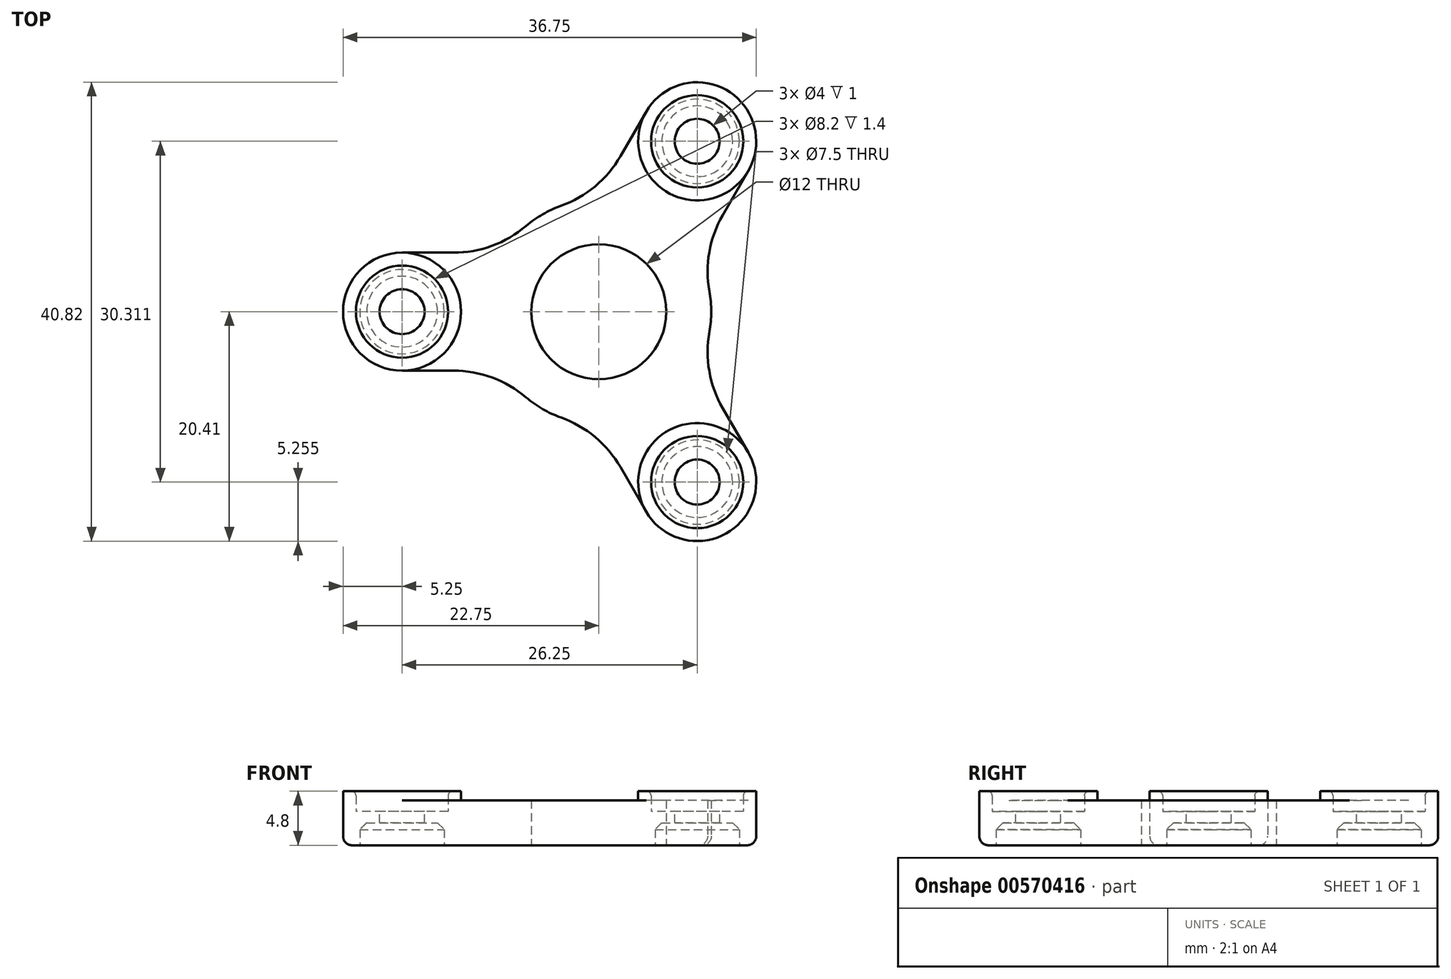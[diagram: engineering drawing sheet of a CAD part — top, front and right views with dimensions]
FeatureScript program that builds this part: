
annotation { "Feature Type Name" : "Feature", "Feature Type Description" : "" }
export const myFeature = defineFeature(function(context is Context, id is Id, definition is map)
    precondition{}
    {
        {
            var Q0;
            Q0=qCreatedBy(makeId("Top.planeOp"),FACE);
            var sketch = newSketch(context, id + "F0", { "sketchPlane" : qUnion([Q0])});
            skArc(sketch, "E0", {"start": v(-17.5, 0) * mm, "mid": v(8.75, -15.16) * mm, "end": v(8.75, 15.16) * mm, "construction": true});
            skLineSegment(sketch, "E1", {"start": v(-17.5, 0) * mm, "end": v(17.5, 0) * mm, "construction": true});
            skLineSegment(sketch, "E2", {"start": v(0, 17.5) * mm, "end": v(0, -17.5) * mm, "construction": true});
            skCircle(sketch, "E3", {"center": v(-17.5, 0) * mm, "radius": 11 * mm, "construction": true});
            skCircle(sketch, "E4", {"center": v(0, 0) * mm, "radius": 10 * mm});
            skCircle(sketch, "E5", {"center": v(-17.5, 0) * mm, "radius": 5.25 * mm});
            skPoint(sketch, "E6.center", {"position": v(-0.38, 0.43) * mm});
            skPoint(sketch, "E7.center", {"position": v(0.72, 3.29) * mm});
            skCircle(sketch, "E8", {"center": v(0, 0) * mm, "radius": 28.5 * mm, "construction": true});
            skPoint(sketch, "E9.orphan", {"position": v(-2.14, 9.77) * mm});
            skPoint(sketch, "E10.orphan", {"position": v(18.22, 8.85) * mm});
            skPoint(sketch, "E11.orphan", {"position": v(12.53, 1.01) * mm});
            skPoint(sketch, "E12.orphan", {"position": v(-7.15, -5.8) * mm});
            skPoint(sketch, "E13.orphan", {"position": v(-2.14, -9.77) * mm});
            skCircle(sketch, "E14", {"center": v(0, 0) * mm, "radius": 6 * mm});
            skArc(sketch, "E15.trimOffspring", {"start": v(2.11, 17.37) * mm, "mid": v(-9.5, 14.7) * mm, "end": v(-16.71, 5.2) * mm, "construction": true});
            skLineSegment(sketch, "E16", {"start": v(-17.5, 0) * mm, "end": v(-17.5, 5.25) * mm, "construction": true});
            skLineSegment(sketch, "E17", {"start": v(-17.5, 5.25) * mm, "end": v(-8.51, 5.25) * mm});
            skLineSegment(sketch, "E18.MirrorCS", {"start": v(-17.5, -5.25) * mm, "end": v(-8.51, -5.25) * mm});
            skCircle(sketch, "E19.1.0", {"center": v(8.75, -15.16) * mm, "radius": 11 * mm, "construction": true});
            skCircle(sketch, "E19.1.1", {"center": v(8.75, -15.16) * mm, "radius": 5.25 * mm});
            skLineSegment(sketch, "E19.1.2", {"start": v(13.3, -12.53) * mm, "end": v(8.8, -4.75) * mm});
            skLineSegment(sketch, "E19.1.3", {"start": v(4.2, -17.78) * mm, "end": v(-0.3, -10) * mm});
            skLineSegment(sketch, "E19.1.4", {"start": v(8.75, -15.16) * mm, "end": v(-8.75, 15.16) * mm, "construction": true});
            skCircle(sketch, "E19.2.0", {"center": v(8.75, 15.16) * mm, "radius": 11 * mm, "construction": true});
            skCircle(sketch, "E19.2.1", {"center": v(8.75, 15.16) * mm, "radius": 5.25 * mm});
            skLineSegment(sketch, "E19.2.2", {"start": v(4.2, 17.78) * mm, "end": v(-0.3, 10) * mm});
            skLineSegment(sketch, "E19.2.3", {"start": v(13.3, 12.53) * mm, "end": v(8.8, 4.75) * mm});
            skLineSegment(sketch, "E19.2.4", {"start": v(8.75, 15.16) * mm, "end": v(-8.75, -15.16) * mm, "construction": true});
            skSolve(sketch);
        }
        {
            var Q0;
            Q0=makeQuery(id+"F0.imprint","IMPRINT",FACE,{"disambiguationData":[TD([[makeQuery(id+"F0.imprint","IMPRINT",EDGE,{"derivedFrom":sQuery(id+"F0.wireOp",EDGE,"E14")}),-1.0]])]});
            var Q1;
            {var subQ0=sQuery(id+"F0.wireOp",EDGE,"E17");Q1=makeQuery(id+"F0.imprint","IMPRINT",FACE,{"disambiguationData":[TD([[makeQuery(id+"F0.imprint","IMPRINT",EDGE,{"derivedFrom":subQ0}),-1.0]])]});}
            var Q2;
            {var subQ0=sQuery(id+"F0.wireOp",EDGE,"E5");var subQ1=makeQuery(id+"F0.imprint","INTERSECT",VERTEX,{"derivedFrom":[subQ0,sQuery(id+"F0.wireOp",EDGE,"E17")]});Q2=makeQuery(id+"F0.imprint","IMPRINT",FACE,{"disambiguationData":[TD([[makeQuery(id+"F0.imprint","IMPRINT",EDGE,{"disambiguationData":[TD([[subQ1,-1.0]])],"derivedFrom":subQ0}),1.0]])]});}
            var Q3;
            {var subQ0=sQuery(id+"F0.wireOp",EDGE,"E19.2.1");var subQ1=makeQuery(id+"F0.imprint","INTERSECT",VERTEX,{"derivedFrom":[subQ0,sQuery(id+"F0.wireOp",EDGE,"E19.2.2")]});Q3=makeQuery(id+"F0.imprint","IMPRINT",FACE,{"disambiguationData":[TD([[makeQuery(id+"F0.imprint","IMPRINT",EDGE,{"disambiguationData":[TD([[subQ1,1.0]])],"derivedFrom":subQ0}),1.0]])]});}
            var Q4;
            {var subQ0=sQuery(id+"F0.wireOp",EDGE,"E19.2.2");Q4=makeQuery(id+"F0.imprint","IMPRINT",FACE,{"disambiguationData":[TD([[makeQuery(id+"F0.imprint","IMPRINT",EDGE,{"derivedFrom":subQ0}),1.0]])]});}
            var Q5;
            {var subQ0=sQuery(id+"F0.wireOp",EDGE,"E19.1.2");Q5=makeQuery(id+"F0.imprint","IMPRINT",FACE,{"disambiguationData":[TD([[makeQuery(id+"F0.imprint","IMPRINT",EDGE,{"derivedFrom":subQ0}),1.0]])]});}
            var Q6;
            {var subQ0=sQuery(id+"F0.wireOp",EDGE,"E19.1.1");var subQ1=makeQuery(id+"F0.imprint","INTERSECT",VERTEX,{"derivedFrom":[subQ0,sQuery(id+"F0.wireOp",EDGE,"E19.1.2")]});Q6=makeQuery(id+"F0.imprint","IMPRINT",FACE,{"disambiguationData":[TD([[makeQuery(id+"F0.imprint","IMPRINT",EDGE,{"disambiguationData":[TD([[subQ1,1.0]])],"derivedFrom":subQ0}),1.0]])]});}
            extrude(context, id + "F1", {"entities" : qUnion([Q0, Q1, Q2, Q3, Q4, Q5, Q6]), "depth" : 4 * mm, "offsetDistance" : 25 * mm});
        }
        {
            var Q0;
            Q0=makeQuery(id+"F1.opExtrude","CAP_FACE",FACE,{"disambiguationData":[OSD([sQuery(id+"F0.wireOp",EDGE,"E4"),sQuery(id+"F0.wireOp",EDGE,"E5"),sQuery(id+"F0.wireOp",EDGE,"E6.1.0"),sQuery(id+"F0.wireOp",EDGE,"E6.2.0"),sQuery(id+"F0.wireOp",EDGE,"E14"),sQuery(id+"F0.wireOp",EDGE,"E17"),sQuery(id+"F0.wireOp",EDGE,"E18.MirrorCS"),sQuery(id+"F0.wireOp",EDGE,"43669a28-cf5b-415e-ac1e-aebf97da9a9c.1.0"),sQuery(id+"F0.wireOp",EDGE,"43669a28-cf5b-415e-ac1e-aebf97da9a9c.1.1"),sQuery(id+"F0.wireOp",EDGE,"43669a28-cf5b-415e-ac1e-aebf97da9a9c.2.0"),sQuery(id+"F0.wireOp",EDGE,"43669a28-cf5b-415e-ac1e-aebf97da9a9c.2.1")])],"isStart":false});
            var sketch = newSketch(context, id + "F2", { "sketchPlane" : qUnion([Q0])});
            skCircle(sketch, "E20.0", {"center": v(-17.5, 0) * mm, "radius": 5.25 * mm});
            skCircle(sketch, "E21", {"center": v(-17.5, 0) * mm, "radius": 4.1 * mm});
            skCircle(sketch, "E22.1.0", {"center": v(8.75, -15.16) * mm, "radius": 5.25 * mm});
            skCircle(sketch, "E22.1.1", {"center": v(8.75, -15.16) * mm, "radius": 4.1 * mm});
            skCircle(sketch, "E22.2.0", {"center": v(8.75, 15.16) * mm, "radius": 5.25 * mm});
            skCircle(sketch, "E22.2.1", {"center": v(8.75, 15.16) * mm, "radius": 4.1 * mm});
            skPoint(sketch, "E22.center", {"position": v(0, 0) * mm});
            skCircle(sketch, "E23", {"center": v(-17.5, 0) * mm, "radius": 2 * mm});
            skCircle(sketch, "E24.1.0", {"center": v(8.75, -15.16) * mm, "radius": 2 * mm});
            skCircle(sketch, "E24.2.0", {"center": v(8.75, 15.16) * mm, "radius": 2 * mm});
            skSolve(sketch);
        }
        {
            var Q0;
            Q0=makeQuery(id+"F2.imprint","IMPRINT",FACE,{"disambiguationData":[TD([[makeQuery(id+"F2.imprint","IMPRINT",EDGE,{"derivedFrom":sQuery(id+"F2.wireOp",EDGE,"E21")}),-1.0]])]});
            var Q1;
            Q1=makeQuery(id+"F2.imprint","IMPRINT",FACE,{"disambiguationData":[TD([[makeQuery(id+"F2.imprint","IMPRINT",EDGE,{"derivedFrom":sQuery(id+"F2.wireOp",EDGE,"E22.2.0")}),1.0]])]});
            var Q2;
            Q2=makeQuery(id+"F2.imprint","IMPRINT",FACE,{"disambiguationData":[TD([[makeQuery(id+"F2.imprint","IMPRINT",EDGE,{"derivedFrom":sQuery(id+"F2.wireOp",EDGE,"E22.1.0")}),1.0]])]});
            extrude(context, id + "F3", {"entities" : qUnion([Q0, Q1, Q2]), "operationType" : NewBodyOperationType.ADD, "depth" : .8 * mm, "offsetDistance" : 25 * mm});
        }
        {
            var Q0;
            Q0=makeQuery(id+"F2.imprint","IMPRINT",FACE,{"disambiguationData":[TD([[makeQuery(id+"F2.imprint","IMPRINT",EDGE,{"derivedFrom":sQuery(id+"F2.wireOp",EDGE,"E23")}),1.0]])]});
            var Q1;
            Q1=makeQuery(id+"F2.imprint","IMPRINT",FACE,{"disambiguationData":[TD([[makeQuery(id+"F2.imprint","IMPRINT",EDGE,{"derivedFrom":sQuery(id+"F2.wireOp",EDGE,"E24.2.0")}),1.0]])]});
            var Q2;
            Q2=makeQuery(id+"F2.imprint","IMPRINT",FACE,{"disambiguationData":[TD([[makeQuery(id+"F2.imprint","IMPRINT",EDGE,{"derivedFrom":sQuery(id+"F2.wireOp",EDGE,"E24.1.0")}),1.0]])]});
            extrude(context, id + "F4", {"entities" : qUnion([Q0, Q1, Q2]), "operationType" : NewBodyOperationType.REMOVE, "endBound" : BoundingType.THROUGH_ALL, "oppositeDirection" : true, "depth" : 25 * mm, "offsetDistance" : 25 * mm});
        }
        {
            var Q0;
            Q0=makeQuery(id+"F1.opExtrude","CAP_FACE",FACE,{"disambiguationData":[OSD([sQuery(id+"F0.wireOp",EDGE,"E4"),sQuery(id+"F0.wireOp",EDGE,"E5"),sQuery(id+"F0.wireOp",EDGE,"E6.1.0"),sQuery(id+"F0.wireOp",EDGE,"E6.2.0"),sQuery(id+"F0.wireOp",EDGE,"E14"),sQuery(id+"F0.wireOp",EDGE,"E17"),sQuery(id+"F0.wireOp",EDGE,"E18.MirrorCS"),sQuery(id+"F0.wireOp",EDGE,"43669a28-cf5b-415e-ac1e-aebf97da9a9c.1.0"),sQuery(id+"F0.wireOp",EDGE,"43669a28-cf5b-415e-ac1e-aebf97da9a9c.1.1"),sQuery(id+"F0.wireOp",EDGE,"43669a28-cf5b-415e-ac1e-aebf97da9a9c.2.0"),sQuery(id+"F0.wireOp",EDGE,"43669a28-cf5b-415e-ac1e-aebf97da9a9c.2.1")])],"isStart":true});
            var sketch = newSketch(context, id + "F5", { "sketchPlane" : qUnion([Q0])});
            skCircle(sketch, "E25.0", {"center": v(-17.5, 0) * mm, "radius": 2 * mm, "construction": true});
            skCircle(sketch, "E26", {"center": v(-17.5, 0) * mm, "radius": 3.75 * mm});
            skCircle(sketch, "E27.1.0", {"center": v(8.75, -15.16) * mm, "radius": 3.75 * mm});
            skCircle(sketch, "E27.2.0", {"center": v(8.75, 15.16) * mm, "radius": 3.75 * mm});
            skPoint(sketch, "E27.center", {"position": v(0, 0) * mm});
            skSolve(sketch);
        }
        {
            var Q0;
            Q0=makeQuery(id+"F5.imprint","IMPRINT",FACE,{"disambiguationData":[TD([[makeQuery(id+"F5.imprint","IMPRINT",EDGE,{"derivedFrom":sQuery(id+"F5.wireOp",EDGE,"E26")}),1.0]])]});
            var Q1;
            Q1=makeQuery(id+"F5.imprint","IMPRINT",FACE,{"disambiguationData":[TD([[makeQuery(id+"F5.imprint","IMPRINT",EDGE,{"derivedFrom":sQuery(id+"F5.wireOp",EDGE,"E27.2.0")}),1.0]])]});
            var Q2;
            Q2=makeQuery(id+"F5.imprint","IMPRINT",FACE,{"disambiguationData":[TD([[makeQuery(id+"F5.imprint","IMPRINT",EDGE,{"derivedFrom":sQuery(id+"F5.wireOp",EDGE,"E27.1.0")}),1.0]])]});
            extrude(context, id + "F6", {"entities" : qUnion([Q0, Q1, Q2]), "operationType" : NewBodyOperationType.REMOVE, "oppositeDirection" : true, "depth" : 2 * mm, "offsetDistance" : 25 * mm});
        }
        {
            var Q0;
            Q0=makeQuery(id+"F6.boolean.opBoolean","COPY",EDGE,{"derivedFrom":makeQuery(id+"F6.opExtrude","CAP_EDGE",EDGE,{"disambiguationData":[OSD([sQuery(id+"F5.wireOp",EDGE,"E27.2.0")])],"isStart":false})});
            var Q1;
            Q1=makeQuery(id+"F6.boolean.opBoolean","COPY",EDGE,{"derivedFrom":makeQuery(id+"F6.opExtrude","CAP_EDGE",EDGE,{"disambiguationData":[OSD([sQuery(id+"F5.wireOp",EDGE,"E26")])],"isStart":false})});
            var Q2;
            Q2=makeQuery(id+"F6.boolean.opBoolean","COPY",EDGE,{"derivedFrom":makeQuery(id+"F6.opExtrude","CAP_EDGE",EDGE,{"disambiguationData":[OSD([sQuery(id+"F5.wireOp",EDGE,"E27.1.0")])],"isStart":false})});
            chamfer(context, id + "F7", {"entities" : qUnion([Q0, Q1, Q2]), "width" : .6 * mm, "tangentPropagation" : true});
        }
        {
            var Q0;
            Q0=makeQuery(id+"F3.boolean.opBoolean","SPLIT",FACE,{"disambiguationData":[TD([makeQuery(id+"F3.opExtrude","SWEPT_FACE",FACE,{"disambiguationData":[OSD([sQuery(id+"F2.wireOp",EDGE,"E21")])]})])],"derivedFrom":makeQuery(id+"F1.opExtrude","CAP_FACE",FACE,{"disambiguationData":[OSD([sQuery(id+"F0.wireOp",EDGE,"E4"),sQuery(id+"F0.wireOp",EDGE,"E5"),sQuery(id+"F0.wireOp",EDGE,"E6.1.0"),sQuery(id+"F0.wireOp",EDGE,"E6.2.0"),sQuery(id+"F0.wireOp",EDGE,"E14"),sQuery(id+"F0.wireOp",EDGE,"E17"),sQuery(id+"F0.wireOp",EDGE,"E18.MirrorCS"),sQuery(id+"F0.wireOp",EDGE,"43669a28-cf5b-415e-ac1e-aebf97da9a9c.1.0"),sQuery(id+"F0.wireOp",EDGE,"43669a28-cf5b-415e-ac1e-aebf97da9a9c.1.1"),sQuery(id+"F0.wireOp",EDGE,"43669a28-cf5b-415e-ac1e-aebf97da9a9c.2.0"),sQuery(id+"F0.wireOp",EDGE,"43669a28-cf5b-415e-ac1e-aebf97da9a9c.2.1")])],"isStart":false})});
            var Q1;
            Q1=makeQuery(id+"F3.boolean.opBoolean","SPLIT",FACE,{"disambiguationData":[TD([makeQuery(id+"F3.opExtrude","SWEPT_FACE",FACE,{"disambiguationData":[OSD([sQuery(id+"F2.wireOp",EDGE,"E22.2.1")])]})])],"derivedFrom":makeQuery(id+"F1.opExtrude","CAP_FACE",FACE,{"disambiguationData":[OSD([sQuery(id+"F0.wireOp",EDGE,"E4"),sQuery(id+"F0.wireOp",EDGE,"E5"),sQuery(id+"F0.wireOp",EDGE,"E6.1.0"),sQuery(id+"F0.wireOp",EDGE,"E6.2.0"),sQuery(id+"F0.wireOp",EDGE,"E14"),sQuery(id+"F0.wireOp",EDGE,"E17"),sQuery(id+"F0.wireOp",EDGE,"E18.MirrorCS"),sQuery(id+"F0.wireOp",EDGE,"43669a28-cf5b-415e-ac1e-aebf97da9a9c.1.0"),sQuery(id+"F0.wireOp",EDGE,"43669a28-cf5b-415e-ac1e-aebf97da9a9c.1.1"),sQuery(id+"F0.wireOp",EDGE,"43669a28-cf5b-415e-ac1e-aebf97da9a9c.2.0"),sQuery(id+"F0.wireOp",EDGE,"43669a28-cf5b-415e-ac1e-aebf97da9a9c.2.1")])],"isStart":false})});
            var Q2;
            Q2=makeQuery(id+"F3.boolean.opBoolean","SPLIT",FACE,{"disambiguationData":[TD([makeQuery(id+"F3.opExtrude","SWEPT_FACE",FACE,{"disambiguationData":[OSD([sQuery(id+"F2.wireOp",EDGE,"E22.1.1")])]})])],"derivedFrom":makeQuery(id+"F1.opExtrude","CAP_FACE",FACE,{"disambiguationData":[OSD([sQuery(id+"F0.wireOp",EDGE,"E4"),sQuery(id+"F0.wireOp",EDGE,"E5"),sQuery(id+"F0.wireOp",EDGE,"E6.1.0"),sQuery(id+"F0.wireOp",EDGE,"E6.2.0"),sQuery(id+"F0.wireOp",EDGE,"E14"),sQuery(id+"F0.wireOp",EDGE,"E17"),sQuery(id+"F0.wireOp",EDGE,"E18.MirrorCS"),sQuery(id+"F0.wireOp",EDGE,"43669a28-cf5b-415e-ac1e-aebf97da9a9c.1.0"),sQuery(id+"F0.wireOp",EDGE,"43669a28-cf5b-415e-ac1e-aebf97da9a9c.1.1"),sQuery(id+"F0.wireOp",EDGE,"43669a28-cf5b-415e-ac1e-aebf97da9a9c.2.0"),sQuery(id+"F0.wireOp",EDGE,"43669a28-cf5b-415e-ac1e-aebf97da9a9c.2.1")])],"isStart":false})});
            extrude(context, id + "F8", {"entities" : qUnion([Q0, Q1, Q2]), "operationType" : NewBodyOperationType.REMOVE, "oppositeDirection" : true, "depth" : 1 * mm, "offsetDistance" : 25 * mm});
        }
        {
            var Q0;
            Q0=makeQuery(id+"F1.opExtrude","SWEPT_EDGE",EDGE,{"disambiguationData":[OSD([sQuery(id+"F0.wireOp",EDGE,"E4"),sQuery(id+"F0.wireOp",EDGE,"E18.MirrorCS")])]});
            var Q1;
            Q1=makeQuery(id+"F1.opExtrude","SWEPT_EDGE",EDGE,{"disambiguationData":[OSD([sQuery(id+"F0.wireOp",EDGE,"E4"),sQuery(id+"F0.wireOp",EDGE,"43669a28-cf5b-415e-ac1e-aebf97da9a9c.1.0")])]});
            var Q2;
            Q2=makeQuery(id+"F1.opExtrude","SWEPT_EDGE",EDGE,{"disambiguationData":[OSD([sQuery(id+"F0.wireOp",EDGE,"E4"),sQuery(id+"F0.wireOp",EDGE,"43669a28-cf5b-415e-ac1e-aebf97da9a9c.1.1")])]});
            var Q3;
            Q3=makeQuery(id+"F1.opExtrude","SWEPT_EDGE",EDGE,{"disambiguationData":[OSD([sQuery(id+"F0.wireOp",EDGE,"E4"),sQuery(id+"F0.wireOp",EDGE,"43669a28-cf5b-415e-ac1e-aebf97da9a9c.2.0")])]});
            var Q4;
            Q4=makeQuery(id+"F1.opExtrude","SWEPT_EDGE",EDGE,{"disambiguationData":[OSD([sQuery(id+"F0.wireOp",EDGE,"E4"),sQuery(id+"F0.wireOp",EDGE,"E17")])]});
            var Q5;
            Q5=makeQuery(id+"F1.opExtrude","SWEPT_EDGE",EDGE,{"disambiguationData":[OSD([sQuery(id+"F0.wireOp",EDGE,"E4"),sQuery(id+"F0.wireOp",EDGE,"43669a28-cf5b-415e-ac1e-aebf97da9a9c.2.1")])]});
            fillet(context, id + "F9", {"entities" : qUnion([Q0, Q1, Q2, Q3, Q4, Q5]), "radius" : 10 * mm, "tangentPropagation" : true, "allowEdgeOverflow" : false});
        }
        {
            var Q0;
            {var subQ0=sQuery(id+"F0.wireOp",EDGE,"E18.MirrorCS");var subQ1=sQuery(id+"F0.wireOp",EDGE,"E17");var subQ2=sQuery(id+"F0.wireOp",EDGE,"E14");var subQ3=sQuery(id+"F0.wireOp",EDGE,"E6.2.0");var subQ4=sQuery(id+"F0.wireOp",EDGE,"E6.1.0");var subQ5=sQuery(id+"F0.wireOp",EDGE,"43669a28-cf5b-415e-ac1e-aebf97da9a9c.1.0");var subQ6=sQuery(id+"F0.wireOp",EDGE,"E4");var subQ7=sQuery(id+"F0.wireOp",EDGE,"43669a28-cf5b-415e-ac1e-aebf97da9a9c.2.1");var subQ8=sQuery(id+"F0.wireOp",EDGE,"E5");var subQ9=sQuery(id+"F0.wireOp",EDGE,"43669a28-cf5b-415e-ac1e-aebf97da9a9c.1.1");var subQ10=sQuery(id+"F0.wireOp",EDGE,"43669a28-cf5b-415e-ac1e-aebf97da9a9c.2.0");Q0=makeQuery(id+"F3.boolean.opBoolean","SPLIT",FACE,{"disambiguationData":[TD([makeQuery(id+"F1.opExtrude","SWEPT_FACE",FACE,{"disambiguationData":[OSD([subQ8])]})])],"derivedFrom":makeQuery(id+"F1.opExtrude","CAP_FACE",FACE,{"disambiguationData":[OSD([subQ6,subQ8,subQ4,subQ3,subQ2,subQ1,subQ0,subQ5,subQ9,subQ10,subQ7])],"isStart":false})});}
            var Q1;
            Q1=makeQuery(id+"F3.opExtrude","CAP_EDGE",EDGE,{"disambiguationData":[OSD([sQuery(id+"F2.wireOp",EDGE,"E21")])],"isStart":false});
            var Q2;
            Q2=makeQuery(id+"F3.opExtrude","CAP_EDGE",EDGE,{"disambiguationData":[OSD([sQuery(id+"F2.wireOp",EDGE,"E22.1.1")])],"isStart":false});
            var Q3;
            Q3=makeQuery(id+"F3.opExtrude","CAP_EDGE",EDGE,{"disambiguationData":[OSD([sQuery(id+"F2.wireOp",EDGE,"E22.2.1")])],"isStart":false});
            fillet(context, id + "F10", {"entities" : qUnion([Q0, Q1, Q2, Q3]), "radius" : .4 * mm, "tangentPropagation" : true, "allowEdgeOverflow" : false});
        }
        {
            var Q0;
            {var subQ0=sQuery(id+"F0.wireOp",EDGE,"E18.MirrorCS");var subQ1=sQuery(id+"F0.wireOp",EDGE,"E4");Q0=makeQuery(id+"F9.opFillet","BLEND_EDGE",EDGE,{"blendedFrom":[makeQuery(id+"F1.opExtrude","SWEPT_EDGE",EDGE,{"disambiguationData":[OSD([subQ1,subQ0])]}),makeQuery(id+"F1.opExtrude","CAP_FACE",FACE,{"disambiguationData":[OSD([subQ1,sQuery(id+"F0.wireOp",EDGE,"E5"),sQuery(id+"F0.wireOp",EDGE,"E14"),sQuery(id+"F0.wireOp",EDGE,"E17"),subQ0,sQuery(id+"F0.wireOp",EDGE,"E19.1.1"),sQuery(id+"F0.wireOp",EDGE,"E19.1.2"),sQuery(id+"F0.wireOp",EDGE,"E19.1.3"),sQuery(id+"F0.wireOp",EDGE,"E19.2.1"),sQuery(id+"F0.wireOp",EDGE,"E19.2.2"),sQuery(id+"F0.wireOp",EDGE,"E19.2.3")])],"isStart":true})],"blendedInto":[makeQuery(id+"F1.opExtrude","CAP_FACE",FACE,{"disambiguationData":[OSD([subQ1,sQuery(id+"F0.wireOp",EDGE,"E5"),sQuery(id+"F0.wireOp",EDGE,"E14"),sQuery(id+"F0.wireOp",EDGE,"E17"),subQ0,sQuery(id+"F0.wireOp",EDGE,"E19.1.1"),sQuery(id+"F0.wireOp",EDGE,"E19.1.2"),sQuery(id+"F0.wireOp",EDGE,"E19.1.3"),sQuery(id+"F0.wireOp",EDGE,"E19.2.1"),sQuery(id+"F0.wireOp",EDGE,"E19.2.2"),sQuery(id+"F0.wireOp",EDGE,"E19.2.3")])],"isStart":true})]});}
            fillet(context, id + "F11", {"entities" : qUnion([Q0]), "radius" : .8 * mm, "tangentPropagation" : true, "allowEdgeOverflow" : false});
        }
    });
